# Revit family: Hager-Orion_Plus-IP65-D300-Cl.II-Poly_floor_encl-630A-NoHosted-UK-en
name_source: partatom
category: Electrical Equipment
units: mm (PartAtom-declared; Revit-internal decimal feet)

## family parameters
Always vertical = Yes
Cut with Voids When Loaded = No
Panel Configuration = Two Columns, Circuits Across
Part Type = Panelboard
Room Calculation Point = No
Round Connector Dimension = Use Diameter
Shared = No
Work Plane-Based = Yes

## types (2) — shared parameters
Default Elevation = 1219 mm
EF000003 - Mounting method = EV012274 - Floor installation
EF000007 - Colour = EV000270 - Grey
EF000008 - Width = 850 mm  [stored 2.78871 ft]
EF000040 - Height = 1200 mm  [stored 3.93701 ft]
EF000049 - Depth = 300 mm  [stored 0.984252 ft]
EF000116 - RAL-number = 7035
EF000118 - With mounting plate = No
EF000266 - Number of rows = 7
EF001088 - Extension possible = No
EF001596 - Material housing = EV000139 - Plastic
EF001613 - Circuit integrity = EV000494 - None
EF003532 - Suitable for outdoor use = Yes
EF004427 - Number of modules = 259
EF004464 - Type of door = EV002646 - Single
EF005474 - Degree of protection (IP) = EV006421 - IP65
EF006244 - Transparent cover/door = No
EF006306 - With lock = Yes
EF007800 - Suitable for lightning protection = No
EF008873 - Nominal current (In) = 630 A
EF009170 - Material plate thickness cabinet = 2 mm  [stored 0.00656168 ft]
EF009171 - Material plate thickness door/cover = 2 mm  [stored 0.00656168 ft]
EF015940 - Cover with overpressure release = No
HG000002 - With door or cover = Yes
HG000003 - Range = Orion Plus
HG000006 - Flush mounted = No
HG000009 - Double swing door = No
HG000010 - Asymmetric doors = No
HG000023 - Double section enclosure = No
HG000024 - Bottom section height = 600 mm
HG000026 - Floor standing = Yes
HG000027 - Plinth height = 70 mm  [stored 0.229659 ft]
Manufacturer = Hager
Type Comments = Orion Plus
zero-valued in all types: EF000218 - Built-in depth, EF000437 - Number of conduit inlets, EF002950 - Width in number of modular spacings, EF009554 - Number of openings for flange plates

## per-type parameters (varying)
| type | EF000339 - Type of cover | EF001131 - Internal depth | EF004293 - Impact strength | EF009212 - Cover model | HG000004 - Manufacturer reference |
| Floor installation IP65 W850 H1200 D300  - FL327B | EV001012 - Cover | 300 mm  [stored 0.984252 ft] | EV006814 - IK08 | EV000116 - Closed | FL327B |
| Floor installation IP65 W850 H1200 D300  - FL527B | EV004216 - Door | 235 mm  [stored 0.770997 ft] | EV008784 - IK10 | EV009916 - With notch | FL527B |

note: [stored X ft] marks values corroborated as IEEE doubles in the binary element streams (Revit-internal decimal feet)

## geometry (parser evidence)
native form markers: Blend x4, Sweep x5
no freeform markers — native parametric forms only
